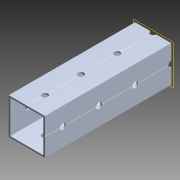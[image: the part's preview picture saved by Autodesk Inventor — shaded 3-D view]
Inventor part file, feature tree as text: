
AUTODESK INVENTOR PART (.ipt)
format: ipt  version: 2014 (Build 180170000, 170)  size: 1,128,448 bytes
history: native  units: in
note: dims shown in document units (in); Inventor stores cm internally (conversion verified against a paired STEP export)
features: pattern_circular x1, other x1, plane x1, extrude x1, imported_body x1, sketch x1
ambient origin geometry x8: Origin, YZ Plane, XZ Plane, XY Plane, X Axis, Y Axis, Z Axis, Center Point
bodies: Body1 (feature_tree)
feature tree (6):
  pattern_circular  "CirPattern2"
  other  "217-3426-STEP1"
  plane  "Work Plane1"
  extrude  "Extrusion1"  Depth=3937.0079in TaperAngle=0.0deg
  imported_body  "Base1"
  sketch  "Sketch1"  dims[d0=-3.5in d1=3937.0079in d2=0.0in]
